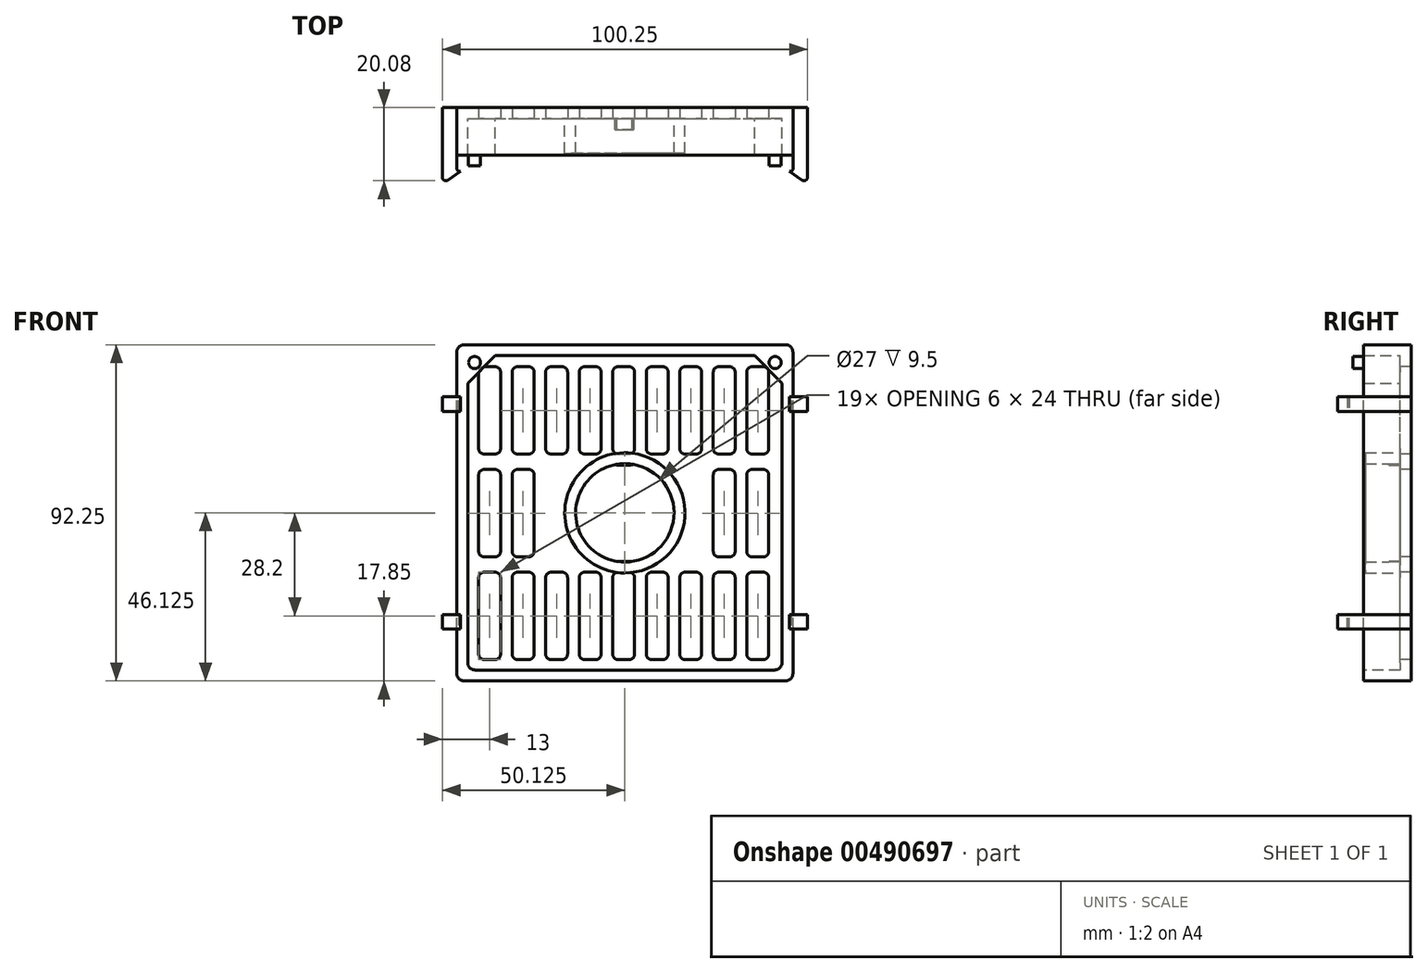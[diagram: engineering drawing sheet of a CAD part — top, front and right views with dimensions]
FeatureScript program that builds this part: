
annotation { "Feature Type Name" : "Feature", "Feature Type Description" : "" }
export const myFeature = defineFeature(function(context is Context, id is Id, definition is map)
    precondition{}
    {
        {
            var Q0;
            Q0=qCreatedBy(makeId("Front.planeOp"),FACE);
            var sketch = newSketch(context, id + "F0", { "sketchPlane" : qUnion([Q0])});
            skLineSegment(sketch, "E0.bottom", {"start": v(0, 0) * mm, "end": v(92.25, 0) * mm});
            skLineSegment(sketch, "E0.top", {"start": v(0, 92.25) * mm, "end": v(92.25, 92.25) * mm});
            skLineSegment(sketch, "E0.left", {"start": v(0, 0) * mm, "end": v(0, 92.25) * mm});
            skLineSegment(sketch, "E0.right", {"start": v(92.25, 0) * mm, "end": v(92.25, 92.25) * mm});
            skSolve(sketch);
        }
        {
            var Q0;
            Q0 = qSketchRegion(id + "F0", true);
            extrude(context, id + "F1", {"entities" : qUnion([Q0]), "depth" : 13 * mm, "offsetDistance" : 25 * mm});
        }
        {
            var Q0;
            Q0=makeQuery(id+"F1.opExtrude","SWEPT_EDGE",EDGE,{"disambiguationData":[OSD([sQuery(id+"F0.wireOp",EDGE,"E0.top"),sQuery(id+"F0.wireOp",EDGE,"E0.right")])]});
            var Q1;
            Q1=makeQuery(id+"F1.opExtrude","SWEPT_EDGE",EDGE,{"disambiguationData":[OSD([sQuery(id+"F0.wireOp",EDGE,"E0.top"),sQuery(id+"F0.wireOp",EDGE,"E0.left")])]});
            var Q2;
            Q2=makeQuery(id+"F1.opExtrude","SWEPT_EDGE",EDGE,{"disambiguationData":[OSD([sQuery(id+"F0.wireOp",EDGE,"E0.bottom"),sQuery(id+"F0.wireOp",EDGE,"E0.left")])]});
            var Q3;
            Q3=makeQuery(id+"F1.opExtrude","SWEPT_EDGE",EDGE,{"disambiguationData":[OSD([sQuery(id+"F0.wireOp",EDGE,"E0.bottom"),sQuery(id+"F0.wireOp",EDGE,"E0.right")])]});
            fillet(context, id + "F2", {"entities" : qUnion([Q0, Q1, Q2, Q3]), "radius" : 2 * mm, "tangentPropagation" : true, "allowEdgeOverflow" : false});
        }
        {
            var Q0;
            Q0=makeQuery(id+"F1.opExtrude","CAP_FACE",FACE,{"disambiguationData":[OSD([sQuery(id+"F0.wireOp",EDGE,"E0.bottom"),sQuery(id+"F0.wireOp",EDGE,"E0.top"),sQuery(id+"F0.wireOp",EDGE,"E0.left"),sQuery(id+"F0.wireOp",EDGE,"E0.right")])],"isStart":false});
            shell(context, id + "F3", {"entities" : qUnion([Q0]), "thickness" : 3 * mm});
        }
        {
            var Q0;
            Q0=makeQuery(id+"F3.opShell","OFFSET_FACE",FACE,{"disambiguationData":[OSD([sQuery(id+"F0.wireOp",EDGE,"E0.bottom"),sQuery(id+"F0.wireOp",EDGE,"E0.top"),sQuery(id+"F0.wireOp",EDGE,"E0.left"),sQuery(id+"F0.wireOp",EDGE,"E0.right")])]});
            var sketch = newSketch(context, id + "F4", { "sketchPlane" : qUnion([Q0])});
            skLineSegment(sketch, "E1", {"start": v(46.12, 89.25) * mm, "end": v(46.12, 3) * mm, "construction": true});
            skLineSegment(sketch, "E2", {"start": v(3, 46.12) * mm, "end": v(89.25, 46.12) * mm, "construction": true});
            skCircle(sketch, "E3", {"center": v(46.12, 46.12) * mm, "radius": 16.5 * mm});
            skSolve(sketch);
        }
        {
            var Q0;
            Q0 = qSketchRegion(id + "F4", true);
            extrude(context, id + "F5", {"entities" : qUnion([Q0]), "operationType" : NewBodyOperationType.ADD, "depth" : 9.5 * mm, "offsetDistance" : 25 * mm});
        }
        {
            var Q0;
            Q0=makeQuery(id+"F3.opShell","OFFSET_FACE",FACE,{"disambiguationData":[OSD([sQuery(id+"F0.wireOp",EDGE,"E0.bottom"),sQuery(id+"F0.wireOp",EDGE,"E0.top"),sQuery(id+"F0.wireOp",EDGE,"E0.left"),sQuery(id+"F0.wireOp",EDGE,"E0.right")])]});
            var sketch = newSketch(context, id + "F6", { "sketchPlane" : qUnion([Q0])});
            skLineSegment(sketch, "E4.bottom", {"start": v(7.5, 62.25) * mm, "end": v(10.5, 62.25) * mm});
            skLineSegment(sketch, "E4.top", {"start": v(7.5, 86.25) * mm, "end": v(10.5, 86.25) * mm});
            skLineSegment(sketch, "E4.left", {"start": v(6, 63.75) * mm, "end": v(6, 84.75) * mm});
            skLineSegment(sketch, "E4.right", {"start": v(12, 63.75) * mm, "end": v(12, 84.75) * mm});
            skPoint(sketch, "E5.visualSharp", {"position": v(6, 86.25) * mm});
            skArc(sketch, "E5.filletArc", {"start": v(7.5, 86.25) * mm, "mid": v(6.44, 85.81) * mm, "end": v(6, 84.75) * mm});
            skPoint(sketch, "E6.visualSharp", {"position": v(12, 62.25) * mm});
            skArc(sketch, "E6.filletArc", {"start": v(10.5, 62.25) * mm, "mid": v(11.56, 62.69) * mm, "end": v(12, 63.75) * mm});
            skPoint(sketch, "E7.visualSharp", {"position": v(6, 62.25) * mm});
            skArc(sketch, "E7.filletArc", {"start": v(6, 63.75) * mm, "mid": v(6.44, 62.69) * mm, "end": v(7.5, 62.25) * mm});
            skPoint(sketch, "E8.visualSharp", {"position": v(12, 86.25) * mm});
            skArc(sketch, "E8.filletArc", {"start": v(12, 84.75) * mm, "mid": v(11.56, 85.81) * mm, "end": v(10.5, 86.25) * mm});
            skPoint(sketch, "E9.0.1.0", {"position": v(12, 34.05) * mm});
            skPoint(sketch, "E9.0.1.1", {"position": v(6, 34.05) * mm});
            skPoint(sketch, "E9.0.1.2", {"position": v(12, 58.05) * mm});
            skLineSegment(sketch, "E9.0.1.3", {"start": v(12, 35.55) * mm, "end": v(12, 56.55) * mm});
            skPoint(sketch, "E9.0.1.4", {"position": v(6, 58.05) * mm});
            skLineSegment(sketch, "E9.0.1.5", {"start": v(6, 35.55) * mm, "end": v(6, 56.55) * mm});
            skLineSegment(sketch, "E9.0.1.6", {"start": v(7.5, 34.05) * mm, "end": v(10.5, 34.05) * mm});
            skArc(sketch, "E9.0.1.7", {"start": v(7.5, 58.05) * mm, "mid": v(6.44, 57.61) * mm, "end": v(6, 56.55) * mm});
            skArc(sketch, "E9.0.1.8", {"start": v(10.5, 34.05) * mm, "mid": v(11.56, 34.49) * mm, "end": v(12, 35.55) * mm});
            skLineSegment(sketch, "E9.0.1.9", {"start": v(7.5, 58.05) * mm, "end": v(10.5, 58.05) * mm});
            skArc(sketch, "E9.0.1.10", {"start": v(12, 56.55) * mm, "mid": v(11.56, 57.61) * mm, "end": v(10.5, 58.05) * mm});
            skArc(sketch, "E9.0.1.11", {"start": v(6, 35.55) * mm, "mid": v(6.44, 34.49) * mm, "end": v(7.5, 34.05) * mm});
            skPoint(sketch, "E9.0.2.0", {"position": v(12, 5.85) * mm});
            skPoint(sketch, "E9.0.2.1", {"position": v(6, 5.85) * mm});
            skPoint(sketch, "E9.0.2.2", {"position": v(12, 29.85) * mm});
            skLineSegment(sketch, "E9.0.2.3", {"start": v(12, 7.35) * mm, "end": v(12, 28.35) * mm});
            skPoint(sketch, "E9.0.2.4", {"position": v(6, 29.85) * mm});
            skLineSegment(sketch, "E9.0.2.5", {"start": v(6, 7.35) * mm, "end": v(6, 28.35) * mm});
            skLineSegment(sketch, "E9.0.2.6", {"start": v(7.5, 5.85) * mm, "end": v(10.5, 5.85) * mm});
            skArc(sketch, "E9.0.2.7", {"start": v(7.5, 29.85) * mm, "mid": v(6.44, 29.41) * mm, "end": v(6, 28.35) * mm});
            skArc(sketch, "E9.0.2.8", {"start": v(10.5, 5.85) * mm, "mid": v(11.56, 6.29) * mm, "end": v(12, 7.35) * mm});
            skLineSegment(sketch, "E9.0.2.9", {"start": v(7.5, 29.85) * mm, "end": v(10.5, 29.85) * mm});
            skArc(sketch, "E9.0.2.10", {"start": v(12, 28.35) * mm, "mid": v(11.56, 29.41) * mm, "end": v(10.5, 29.85) * mm});
            skArc(sketch, "E9.0.2.11", {"start": v(6, 7.35) * mm, "mid": v(6.44, 6.29) * mm, "end": v(7.5, 5.85) * mm});
            skPoint(sketch, "E9.1.0.0", {"position": v(21.2, 62.25) * mm});
            skPoint(sketch, "E9.1.0.1", {"position": v(15.2, 62.25) * mm});
            skPoint(sketch, "E9.1.0.2", {"position": v(21.2, 86.25) * mm});
            skLineSegment(sketch, "E9.1.0.3", {"start": v(21.2, 63.75) * mm, "end": v(21.2, 84.75) * mm});
            skPoint(sketch, "E9.1.0.4", {"position": v(15.2, 86.25) * mm});
            skLineSegment(sketch, "E9.1.0.5", {"start": v(15.2, 63.75) * mm, "end": v(15.2, 84.75) * mm});
            skLineSegment(sketch, "E9.1.0.6", {"start": v(16.7, 62.25) * mm, "end": v(19.7, 62.25) * mm});
            skArc(sketch, "E9.1.0.7", {"start": v(16.7, 86.25) * mm, "mid": v(15.64, 85.81) * mm, "end": v(15.2, 84.75) * mm});
            skArc(sketch, "E9.1.0.8", {"start": v(19.7, 62.25) * mm, "mid": v(20.76, 62.69) * mm, "end": v(21.2, 63.75) * mm});
            skLineSegment(sketch, "E9.1.0.9", {"start": v(16.7, 86.25) * mm, "end": v(19.7, 86.25) * mm});
            skArc(sketch, "E9.1.0.10", {"start": v(21.2, 84.75) * mm, "mid": v(20.76, 85.81) * mm, "end": v(19.7, 86.25) * mm});
            skArc(sketch, "E9.1.0.11", {"start": v(15.2, 63.75) * mm, "mid": v(15.64, 62.69) * mm, "end": v(16.7, 62.25) * mm});
            skPoint(sketch, "E9.1.1.0", {"position": v(21.2, 34.05) * mm});
            skPoint(sketch, "E9.1.1.1", {"position": v(15.2, 34.05) * mm});
            skPoint(sketch, "E9.1.1.2", {"position": v(21.2, 58.05) * mm});
            skLineSegment(sketch, "E9.1.1.3", {"start": v(21.2, 35.55) * mm, "end": v(21.2, 56.55) * mm});
            skPoint(sketch, "E9.1.1.4", {"position": v(15.2, 58.05) * mm});
            skLineSegment(sketch, "E9.1.1.5", {"start": v(15.2, 35.55) * mm, "end": v(15.2, 56.55) * mm});
            skLineSegment(sketch, "E9.1.1.6", {"start": v(16.7, 34.05) * mm, "end": v(19.7, 34.05) * mm});
            skArc(sketch, "E9.1.1.7", {"start": v(16.7, 58.05) * mm, "mid": v(15.64, 57.61) * mm, "end": v(15.2, 56.55) * mm});
            skArc(sketch, "E9.1.1.8", {"start": v(19.7, 34.05) * mm, "mid": v(20.76, 34.49) * mm, "end": v(21.2, 35.55) * mm});
            skLineSegment(sketch, "E9.1.1.9", {"start": v(16.7, 58.05) * mm, "end": v(19.7, 58.05) * mm});
            skArc(sketch, "E9.1.1.10", {"start": v(21.2, 56.55) * mm, "mid": v(20.76, 57.61) * mm, "end": v(19.7, 58.05) * mm});
            skArc(sketch, "E9.1.1.11", {"start": v(15.2, 35.55) * mm, "mid": v(15.64, 34.49) * mm, "end": v(16.7, 34.05) * mm});
            skPoint(sketch, "E9.1.2.0", {"position": v(21.2, 5.85) * mm});
            skPoint(sketch, "E9.1.2.1", {"position": v(15.2, 5.85) * mm});
            skPoint(sketch, "E9.1.2.2", {"position": v(21.2, 29.85) * mm});
            skLineSegment(sketch, "E9.1.2.3", {"start": v(21.2, 7.35) * mm, "end": v(21.2, 28.35) * mm});
            skPoint(sketch, "E9.1.2.4", {"position": v(15.2, 29.85) * mm});
            skLineSegment(sketch, "E9.1.2.5", {"start": v(15.2, 7.35) * mm, "end": v(15.2, 28.35) * mm});
            skLineSegment(sketch, "E9.1.2.6", {"start": v(16.7, 5.85) * mm, "end": v(19.7, 5.85) * mm});
            skArc(sketch, "E9.1.2.7", {"start": v(16.7, 29.85) * mm, "mid": v(15.64, 29.41) * mm, "end": v(15.2, 28.35) * mm});
            skArc(sketch, "E9.1.2.8", {"start": v(19.7, 5.85) * mm, "mid": v(20.76, 6.29) * mm, "end": v(21.2, 7.35) * mm});
            skLineSegment(sketch, "E9.1.2.9", {"start": v(16.7, 29.85) * mm, "end": v(19.7, 29.85) * mm});
            skArc(sketch, "E9.1.2.10", {"start": v(21.2, 28.35) * mm, "mid": v(20.76, 29.41) * mm, "end": v(19.7, 29.85) * mm});
            skArc(sketch, "E9.1.2.11", {"start": v(15.2, 7.35) * mm, "mid": v(15.64, 6.29) * mm, "end": v(16.7, 5.85) * mm});
            skPoint(sketch, "E9.2.0.0", {"position": v(30.4, 62.25) * mm});
            skPoint(sketch, "E9.2.0.1", {"position": v(24.4, 62.25) * mm});
            skPoint(sketch, "E9.2.0.2", {"position": v(30.4, 86.25) * mm});
            skLineSegment(sketch, "E9.2.0.3", {"start": v(30.4, 63.75) * mm, "end": v(30.4, 84.75) * mm});
            skPoint(sketch, "E9.2.0.4", {"position": v(24.4, 86.25) * mm});
            skLineSegment(sketch, "E9.2.0.5", {"start": v(24.4, 63.75) * mm, "end": v(24.4, 84.75) * mm});
            skLineSegment(sketch, "E9.2.0.6", {"start": v(25.9, 62.25) * mm, "end": v(28.9, 62.25) * mm});
            skArc(sketch, "E9.2.0.7", {"start": v(25.9, 86.25) * mm, "mid": v(24.84, 85.81) * mm, "end": v(24.4, 84.75) * mm});
            skArc(sketch, "E9.2.0.8", {"start": v(28.9, 62.25) * mm, "mid": v(29.96, 62.69) * mm, "end": v(30.4, 63.75) * mm});
            skLineSegment(sketch, "E9.2.0.9", {"start": v(25.9, 86.25) * mm, "end": v(28.9, 86.25) * mm});
            skArc(sketch, "E9.2.0.10", {"start": v(30.4, 84.75) * mm, "mid": v(29.96, 85.81) * mm, "end": v(28.9, 86.25) * mm});
            skArc(sketch, "E9.2.0.11", {"start": v(24.4, 63.75) * mm, "mid": v(24.84, 62.69) * mm, "end": v(25.9, 62.25) * mm});
            skPoint(sketch, "E9.2.1.0", {"position": v(30.4, 34.05) * mm});
            skPoint(sketch, "E9.2.1.1", {"position": v(24.4, 34.05) * mm});
            skPoint(sketch, "E9.2.1.2", {"position": v(30.4, 58.05) * mm});
            skLineSegment(sketch, "E9.2.1.3", {"start": v(30.4, 35.55) * mm, "end": v(30.4, 41.13) * mm});
            skPoint(sketch, "E9.2.1.4", {"position": v(24.4, 58.05) * mm});
            skLineSegment(sketch, "E9.2.1.5", {"start": v(24.4, 35.55) * mm, "end": v(24.4, 56.55) * mm});
            skLineSegment(sketch, "E9.2.1.6", {"start": v(25.9, 34.05) * mm, "end": v(28.9, 34.05) * mm});
            skArc(sketch, "E9.2.1.7", {"start": v(25.9, 58.05) * mm, "mid": v(24.84, 57.61) * mm, "end": v(24.4, 56.55) * mm});
            skArc(sketch, "E9.2.1.8", {"start": v(28.9, 34.05) * mm, "mid": v(29.96, 34.49) * mm, "end": v(30.4, 35.55) * mm});
            skLineSegment(sketch, "E9.2.1.9", {"start": v(25.9, 58.05) * mm, "end": v(28.9, 58.05) * mm});
            skArc(sketch, "E9.2.1.10", {"start": v(30.4, 56.55) * mm, "mid": v(29.96, 57.61) * mm, "end": v(28.9, 58.05) * mm});
            skArc(sketch, "E9.2.1.11", {"start": v(24.4, 35.55) * mm, "mid": v(24.84, 34.49) * mm, "end": v(25.9, 34.05) * mm});
            skPoint(sketch, "E9.2.2.0", {"position": v(30.4, 5.85) * mm});
            skPoint(sketch, "E9.2.2.1", {"position": v(24.4, 5.85) * mm});
            skPoint(sketch, "E9.2.2.2", {"position": v(30.4, 29.85) * mm});
            skLineSegment(sketch, "E9.2.2.3", {"start": v(30.4, 7.35) * mm, "end": v(30.4, 28.35) * mm});
            skPoint(sketch, "E9.2.2.4", {"position": v(24.4, 29.85) * mm});
            skLineSegment(sketch, "E9.2.2.5", {"start": v(24.4, 7.35) * mm, "end": v(24.4, 28.35) * mm});
            skLineSegment(sketch, "E9.2.2.6", {"start": v(25.9, 5.85) * mm, "end": v(28.9, 5.85) * mm});
            skArc(sketch, "E9.2.2.7", {"start": v(25.9, 29.85) * mm, "mid": v(24.84, 29.41) * mm, "end": v(24.4, 28.35) * mm});
            skArc(sketch, "E9.2.2.8", {"start": v(28.9, 5.85) * mm, "mid": v(29.96, 6.29) * mm, "end": v(30.4, 7.35) * mm});
            skLineSegment(sketch, "E9.2.2.9", {"start": v(25.9, 29.85) * mm, "end": v(28.9, 29.85) * mm});
            skArc(sketch, "E9.2.2.10", {"start": v(30.4, 28.35) * mm, "mid": v(29.96, 29.41) * mm, "end": v(28.9, 29.85) * mm});
            skArc(sketch, "E9.2.2.11", {"start": v(24.4, 7.35) * mm, "mid": v(24.84, 6.29) * mm, "end": v(25.9, 5.85) * mm});
            skPoint(sketch, "E9.3.0.0", {"position": v(39.6, 62.25) * mm});
            skPoint(sketch, "E9.3.0.1", {"position": v(33.6, 62.25) * mm});
            skPoint(sketch, "E9.3.0.2", {"position": v(39.6, 86.25) * mm});
            skLineSegment(sketch, "E9.3.0.3", {"start": v(39.6, 63.75) * mm, "end": v(39.6, 84.75) * mm});
            skPoint(sketch, "E9.3.0.4", {"position": v(33.6, 86.25) * mm});
            skLineSegment(sketch, "E9.3.0.5", {"start": v(33.6, 63.75) * mm, "end": v(33.6, 84.75) * mm});
            skLineSegment(sketch, "E9.3.0.6", {"start": v(35.1, 62.25) * mm, "end": v(38.1, 62.25) * mm});
            skArc(sketch, "E9.3.0.7", {"start": v(35.1, 86.25) * mm, "mid": v(34.04, 85.81) * mm, "end": v(33.6, 84.75) * mm});
            skArc(sketch, "E9.3.0.8", {"start": v(38.1, 62.25) * mm, "mid": v(39.16, 62.69) * mm, "end": v(39.6, 63.75) * mm});
            skLineSegment(sketch, "E9.3.0.9", {"start": v(35.1, 86.25) * mm, "end": v(38.1, 86.25) * mm});
            skArc(sketch, "E9.3.0.10", {"start": v(39.6, 84.75) * mm, "mid": v(39.16, 85.81) * mm, "end": v(38.1, 86.25) * mm});
            skArc(sketch, "E9.3.0.11", {"start": v(33.6, 63.75) * mm, "mid": v(34.04, 62.69) * mm, "end": v(35.1, 62.25) * mm});
            skPoint(sketch, "E9.3.2.0", {"position": v(39.6, 5.85) * mm});
            skPoint(sketch, "E9.3.2.1", {"position": v(33.6, 5.85) * mm});
            skPoint(sketch, "E9.3.2.2", {"position": v(39.6, 29.85) * mm});
            skLineSegment(sketch, "E9.3.2.3", {"start": v(39.6, 7.35) * mm, "end": v(39.6, 28.35) * mm});
            skPoint(sketch, "E9.3.2.4", {"position": v(33.6, 29.85) * mm});
            skLineSegment(sketch, "E9.3.2.5", {"start": v(33.6, 7.35) * mm, "end": v(33.6, 28.35) * mm});
            skLineSegment(sketch, "E9.3.2.6", {"start": v(35.1, 5.85) * mm, "end": v(38.1, 5.85) * mm});
            skArc(sketch, "E9.3.2.7", {"start": v(35.1, 29.85) * mm, "mid": v(34.04, 29.41) * mm, "end": v(33.6, 28.35) * mm});
            skArc(sketch, "E9.3.2.8", {"start": v(38.1, 5.85) * mm, "mid": v(39.16, 6.29) * mm, "end": v(39.6, 7.35) * mm});
            skLineSegment(sketch, "E9.3.2.9", {"start": v(35.1, 29.85) * mm, "end": v(38.1, 29.85) * mm});
            skArc(sketch, "E9.3.2.10", {"start": v(39.6, 28.35) * mm, "mid": v(39.16, 29.41) * mm, "end": v(38.1, 29.85) * mm});
            skArc(sketch, "E9.3.2.11", {"start": v(33.6, 7.35) * mm, "mid": v(34.04, 6.29) * mm, "end": v(35.1, 5.85) * mm});
            skPoint(sketch, "E9.4.0.0", {"position": v(48.8, 62.25) * mm});
            skPoint(sketch, "E9.4.0.1", {"position": v(42.8, 62.25) * mm});
            skPoint(sketch, "E9.4.0.2", {"position": v(48.8, 86.25) * mm});
            skLineSegment(sketch, "E9.4.0.3", {"start": v(48.8, 63.75) * mm, "end": v(48.8, 84.75) * mm});
            skPoint(sketch, "E9.4.0.4", {"position": v(42.8, 86.25) * mm});
            skLineSegment(sketch, "E9.4.0.5", {"start": v(42.8, 63.75) * mm, "end": v(42.8, 84.75) * mm});
            skLineSegment(sketch, "E9.4.0.6", {"start": v(44.3, 62.25) * mm, "end": v(47.3, 62.25) * mm});
            skArc(sketch, "E9.4.0.7", {"start": v(44.3, 86.25) * mm, "mid": v(43.24, 85.81) * mm, "end": v(42.8, 84.75) * mm});
            skArc(sketch, "E9.4.0.8", {"start": v(47.3, 62.25) * mm, "mid": v(48.36, 62.69) * mm, "end": v(48.8, 63.75) * mm});
            skLineSegment(sketch, "E9.4.0.9", {"start": v(44.3, 86.25) * mm, "end": v(47.3, 86.25) * mm});
            skArc(sketch, "E9.4.0.10", {"start": v(48.8, 84.75) * mm, "mid": v(48.36, 85.81) * mm, "end": v(47.3, 86.25) * mm});
            skArc(sketch, "E9.4.0.11", {"start": v(42.8, 63.75) * mm, "mid": v(43.24, 62.69) * mm, "end": v(44.3, 62.25) * mm});
            skPoint(sketch, "E9.4.2.0", {"position": v(48.8, 5.85) * mm});
            skPoint(sketch, "E9.4.2.1", {"position": v(42.8, 5.85) * mm});
            skPoint(sketch, "E9.4.2.2", {"position": v(48.8, 29.85) * mm});
            skLineSegment(sketch, "E9.4.2.3", {"start": v(48.8, 7.35) * mm, "end": v(48.8, 28.35) * mm});
            skPoint(sketch, "E9.4.2.4", {"position": v(42.8, 29.85) * mm});
            skLineSegment(sketch, "E9.4.2.5", {"start": v(42.8, 7.35) * mm, "end": v(42.8, 28.35) * mm});
            skLineSegment(sketch, "E9.4.2.6", {"start": v(44.3, 5.85) * mm, "end": v(47.3, 5.85) * mm});
            skArc(sketch, "E9.4.2.7", {"start": v(44.3, 29.85) * mm, "mid": v(43.24, 29.41) * mm, "end": v(42.8, 28.35) * mm});
            skArc(sketch, "E9.4.2.8", {"start": v(47.3, 5.85) * mm, "mid": v(48.36, 6.29) * mm, "end": v(48.8, 7.35) * mm});
            skLineSegment(sketch, "E9.4.2.9", {"start": v(44.3, 29.85) * mm, "end": v(47.3, 29.85) * mm});
            skArc(sketch, "E9.4.2.10", {"start": v(48.8, 28.35) * mm, "mid": v(48.36, 29.41) * mm, "end": v(47.3, 29.85) * mm});
            skArc(sketch, "E9.4.2.11", {"start": v(42.8, 7.35) * mm, "mid": v(43.24, 6.29) * mm, "end": v(44.3, 5.85) * mm});
            skPoint(sketch, "E9.5.0.0", {"position": v(58, 62.25) * mm});
            skPoint(sketch, "E9.5.0.1", {"position": v(52, 62.25) * mm});
            skPoint(sketch, "E9.5.0.2", {"position": v(58, 86.25) * mm});
            skLineSegment(sketch, "E9.5.0.3", {"start": v(58, 63.75) * mm, "end": v(58, 84.75) * mm});
            skPoint(sketch, "E9.5.0.4", {"position": v(52, 86.25) * mm});
            skLineSegment(sketch, "E9.5.0.5", {"start": v(52, 63.75) * mm, "end": v(52, 84.75) * mm});
            skLineSegment(sketch, "E9.5.0.6", {"start": v(53.5, 62.25) * mm, "end": v(56.5, 62.25) * mm});
            skArc(sketch, "E9.5.0.7", {"start": v(53.5, 86.25) * mm, "mid": v(52.44, 85.81) * mm, "end": v(52, 84.75) * mm});
            skArc(sketch, "E9.5.0.8", {"start": v(56.5, 62.25) * mm, "mid": v(57.56, 62.69) * mm, "end": v(58, 63.75) * mm});
            skLineSegment(sketch, "E9.5.0.9", {"start": v(53.5, 86.25) * mm, "end": v(56.5, 86.25) * mm});
            skArc(sketch, "E9.5.0.10", {"start": v(58, 84.75) * mm, "mid": v(57.56, 85.81) * mm, "end": v(56.5, 86.25) * mm});
            skArc(sketch, "E9.5.0.11", {"start": v(52, 63.75) * mm, "mid": v(52.44, 62.69) * mm, "end": v(53.5, 62.25) * mm});
            skPoint(sketch, "E9.5.2.0", {"position": v(58, 5.85) * mm});
            skPoint(sketch, "E9.5.2.1", {"position": v(52, 5.85) * mm});
            skPoint(sketch, "E9.5.2.2", {"position": v(58, 29.85) * mm});
            skLineSegment(sketch, "E9.5.2.3", {"start": v(58, 7.35) * mm, "end": v(58, 28.35) * mm});
            skPoint(sketch, "E9.5.2.4", {"position": v(52, 29.85) * mm});
            skLineSegment(sketch, "E9.5.2.5", {"start": v(52, 7.35) * mm, "end": v(52, 28.35) * mm});
            skLineSegment(sketch, "E9.5.2.6", {"start": v(53.5, 5.85) * mm, "end": v(56.5, 5.85) * mm});
            skArc(sketch, "E9.5.2.7", {"start": v(53.5, 29.85) * mm, "mid": v(52.44, 29.41) * mm, "end": v(52, 28.35) * mm});
            skArc(sketch, "E9.5.2.8", {"start": v(56.5, 5.85) * mm, "mid": v(57.56, 6.29) * mm, "end": v(58, 7.35) * mm});
            skLineSegment(sketch, "E9.5.2.9", {"start": v(53.5, 29.85) * mm, "end": v(56.5, 29.85) * mm});
            skArc(sketch, "E9.5.2.10", {"start": v(58, 28.35) * mm, "mid": v(57.56, 29.41) * mm, "end": v(56.5, 29.85) * mm});
            skArc(sketch, "E9.5.2.11", {"start": v(52, 7.35) * mm, "mid": v(52.44, 6.29) * mm, "end": v(53.5, 5.85) * mm});
            skPoint(sketch, "E9.6.0.0", {"position": v(67.2, 62.25) * mm});
            skPoint(sketch, "E9.6.0.1", {"position": v(61.2, 62.25) * mm});
            skPoint(sketch, "E9.6.0.2", {"position": v(67.2, 86.25) * mm});
            skLineSegment(sketch, "E9.6.0.3", {"start": v(67.2, 63.75) * mm, "end": v(67.2, 84.75) * mm});
            skPoint(sketch, "E9.6.0.4", {"position": v(61.2, 86.25) * mm});
            skLineSegment(sketch, "E9.6.0.5", {"start": v(61.2, 63.75) * mm, "end": v(61.2, 84.75) * mm});
            skLineSegment(sketch, "E9.6.0.6", {"start": v(62.7, 62.25) * mm, "end": v(65.7, 62.25) * mm});
            skArc(sketch, "E9.6.0.7", {"start": v(62.7, 86.25) * mm, "mid": v(61.64, 85.81) * mm, "end": v(61.2, 84.75) * mm});
            skArc(sketch, "E9.6.0.8", {"start": v(65.7, 62.25) * mm, "mid": v(66.76, 62.69) * mm, "end": v(67.2, 63.75) * mm});
            skLineSegment(sketch, "E9.6.0.9", {"start": v(62.7, 86.25) * mm, "end": v(65.7, 86.25) * mm});
            skArc(sketch, "E9.6.0.10", {"start": v(67.2, 84.75) * mm, "mid": v(66.76, 85.81) * mm, "end": v(65.7, 86.25) * mm});
            skArc(sketch, "E9.6.0.11", {"start": v(61.2, 63.75) * mm, "mid": v(61.64, 62.69) * mm, "end": v(62.7, 62.25) * mm});
            skPoint(sketch, "E9.6.1.0", {"position": v(67.2, 34.05) * mm});
            skPoint(sketch, "E9.6.1.1", {"position": v(61.2, 34.05) * mm});
            skPoint(sketch, "E9.6.1.2", {"position": v(67.2, 58.05) * mm});
            skLineSegment(sketch, "E9.6.1.3", {"start": v(67.2, 35.55) * mm, "end": v(67.2, 56.55) * mm});
            skPoint(sketch, "E9.6.1.4", {"position": v(61.2, 58.05) * mm});
            skLineSegment(sketch, "E9.6.1.5", {"start": v(61.2, 35.55) * mm, "end": v(61.2, 39.42) * mm});
            skLineSegment(sketch, "E9.6.1.6", {"start": v(62.7, 34.05) * mm, "end": v(65.7, 34.05) * mm});
            skArc(sketch, "E9.6.1.7", {"start": v(62.7, 58.05) * mm, "mid": v(61.64, 57.61) * mm, "end": v(61.2, 56.55) * mm});
            skArc(sketch, "E9.6.1.8", {"start": v(65.7, 34.05) * mm, "mid": v(66.76, 34.49) * mm, "end": v(67.2, 35.55) * mm});
            skLineSegment(sketch, "E9.6.1.9", {"start": v(62.7, 58.05) * mm, "end": v(65.7, 58.05) * mm});
            skArc(sketch, "E9.6.1.10", {"start": v(67.2, 56.55) * mm, "mid": v(66.76, 57.61) * mm, "end": v(65.7, 58.05) * mm});
            skArc(sketch, "E9.6.1.11", {"start": v(61.2, 35.55) * mm, "mid": v(61.64, 34.49) * mm, "end": v(62.7, 34.05) * mm});
            skPoint(sketch, "E9.6.2.0", {"position": v(67.2, 5.85) * mm});
            skPoint(sketch, "E9.6.2.1", {"position": v(61.2, 5.85) * mm});
            skPoint(sketch, "E9.6.2.2", {"position": v(67.2, 29.85) * mm});
            skLineSegment(sketch, "E9.6.2.3", {"start": v(67.2, 7.35) * mm, "end": v(67.2, 28.35) * mm});
            skPoint(sketch, "E9.6.2.4", {"position": v(61.2, 29.85) * mm});
            skLineSegment(sketch, "E9.6.2.5", {"start": v(61.2, 7.35) * mm, "end": v(61.2, 28.35) * mm});
            skLineSegment(sketch, "E9.6.2.6", {"start": v(62.7, 5.85) * mm, "end": v(65.7, 5.85) * mm});
            skArc(sketch, "E9.6.2.7", {"start": v(62.7, 29.85) * mm, "mid": v(61.64, 29.41) * mm, "end": v(61.2, 28.35) * mm});
            skArc(sketch, "E9.6.2.8", {"start": v(65.7, 5.85) * mm, "mid": v(66.76, 6.29) * mm, "end": v(67.2, 7.35) * mm});
            skLineSegment(sketch, "E9.6.2.9", {"start": v(62.7, 29.85) * mm, "end": v(65.7, 29.85) * mm});
            skArc(sketch, "E9.6.2.10", {"start": v(67.2, 28.35) * mm, "mid": v(66.76, 29.41) * mm, "end": v(65.7, 29.85) * mm});
            skArc(sketch, "E9.6.2.11", {"start": v(61.2, 7.35) * mm, "mid": v(61.64, 6.29) * mm, "end": v(62.7, 5.85) * mm});
            skPoint(sketch, "E9.7.0.0", {"position": v(76.4, 62.25) * mm});
            skPoint(sketch, "E9.7.0.1", {"position": v(70.4, 62.25) * mm});
            skPoint(sketch, "E9.7.0.2", {"position": v(76.4, 86.25) * mm});
            skLineSegment(sketch, "E9.7.0.3", {"start": v(76.4, 63.75) * mm, "end": v(76.4, 84.75) * mm});
            skPoint(sketch, "E9.7.0.4", {"position": v(70.4, 86.25) * mm});
            skLineSegment(sketch, "E9.7.0.5", {"start": v(70.4, 63.75) * mm, "end": v(70.4, 84.75) * mm});
            skLineSegment(sketch, "E9.7.0.6", {"start": v(71.9, 62.25) * mm, "end": v(74.9, 62.25) * mm});
            skArc(sketch, "E9.7.0.7", {"start": v(71.9, 86.25) * mm, "mid": v(70.84, 85.81) * mm, "end": v(70.4, 84.75) * mm});
            skArc(sketch, "E9.7.0.8", {"start": v(74.9, 62.25) * mm, "mid": v(75.96, 62.69) * mm, "end": v(76.4, 63.75) * mm});
            skLineSegment(sketch, "E9.7.0.9", {"start": v(71.9, 86.25) * mm, "end": v(74.9, 86.25) * mm});
            skArc(sketch, "E9.7.0.10", {"start": v(76.4, 84.75) * mm, "mid": v(75.96, 85.81) * mm, "end": v(74.9, 86.25) * mm});
            skArc(sketch, "E9.7.0.11", {"start": v(70.4, 63.75) * mm, "mid": v(70.84, 62.69) * mm, "end": v(71.9, 62.25) * mm});
            skPoint(sketch, "E9.7.1.0", {"position": v(76.4, 34.05) * mm});
            skPoint(sketch, "E9.7.1.1", {"position": v(70.4, 34.05) * mm});
            skPoint(sketch, "E9.7.1.2", {"position": v(76.4, 58.05) * mm});
            skLineSegment(sketch, "E9.7.1.3", {"start": v(76.4, 35.55) * mm, "end": v(76.4, 56.55) * mm});
            skPoint(sketch, "E9.7.1.4", {"position": v(70.4, 58.05) * mm});
            skLineSegment(sketch, "E9.7.1.5", {"start": v(70.4, 35.55) * mm, "end": v(70.4, 56.55) * mm});
            skLineSegment(sketch, "E9.7.1.6", {"start": v(71.9, 34.05) * mm, "end": v(74.9, 34.05) * mm});
            skArc(sketch, "E9.7.1.7", {"start": v(71.9, 58.05) * mm, "mid": v(70.84, 57.61) * mm, "end": v(70.4, 56.55) * mm});
            skArc(sketch, "E9.7.1.8", {"start": v(74.9, 34.05) * mm, "mid": v(75.96, 34.49) * mm, "end": v(76.4, 35.55) * mm});
            skLineSegment(sketch, "E9.7.1.9", {"start": v(71.9, 58.05) * mm, "end": v(74.9, 58.05) * mm});
            skArc(sketch, "E9.7.1.10", {"start": v(76.4, 56.55) * mm, "mid": v(75.96, 57.61) * mm, "end": v(74.9, 58.05) * mm});
            skArc(sketch, "E9.7.1.11", {"start": v(70.4, 35.55) * mm, "mid": v(70.84, 34.49) * mm, "end": v(71.9, 34.05) * mm});
            skPoint(sketch, "E9.7.2.0", {"position": v(76.4, 5.85) * mm});
            skPoint(sketch, "E9.7.2.1", {"position": v(70.4, 5.85) * mm});
            skPoint(sketch, "E9.7.2.2", {"position": v(76.4, 29.85) * mm});
            skLineSegment(sketch, "E9.7.2.3", {"start": v(76.4, 7.35) * mm, "end": v(76.4, 28.35) * mm});
            skPoint(sketch, "E9.7.2.4", {"position": v(70.4, 29.85) * mm});
            skLineSegment(sketch, "E9.7.2.5", {"start": v(70.4, 7.35) * mm, "end": v(70.4, 28.35) * mm});
            skLineSegment(sketch, "E9.7.2.6", {"start": v(71.9, 5.85) * mm, "end": v(74.9, 5.85) * mm});
            skArc(sketch, "E9.7.2.7", {"start": v(71.9, 29.85) * mm, "mid": v(70.84, 29.41) * mm, "end": v(70.4, 28.35) * mm});
            skArc(sketch, "E9.7.2.8", {"start": v(74.9, 5.85) * mm, "mid": v(75.96, 6.29) * mm, "end": v(76.4, 7.35) * mm});
            skLineSegment(sketch, "E9.7.2.9", {"start": v(71.9, 29.85) * mm, "end": v(74.9, 29.85) * mm});
            skArc(sketch, "E9.7.2.10", {"start": v(76.4, 28.35) * mm, "mid": v(75.96, 29.41) * mm, "end": v(74.9, 29.85) * mm});
            skArc(sketch, "E9.7.2.11", {"start": v(70.4, 7.35) * mm, "mid": v(70.84, 6.29) * mm, "end": v(71.9, 5.85) * mm});
            skPoint(sketch, "E9.8.0.0", {"position": v(85.6, 62.25) * mm});
            skPoint(sketch, "E9.8.0.1", {"position": v(79.6, 62.25) * mm});
            skPoint(sketch, "E9.8.0.2", {"position": v(85.6, 86.25) * mm});
            skLineSegment(sketch, "E9.8.0.3", {"start": v(85.6, 63.75) * mm, "end": v(85.6, 84.75) * mm});
            skPoint(sketch, "E9.8.0.4", {"position": v(79.6, 86.25) * mm});
            skLineSegment(sketch, "E9.8.0.5", {"start": v(79.6, 63.75) * mm, "end": v(79.6, 84.75) * mm});
            skLineSegment(sketch, "E9.8.0.6", {"start": v(81.1, 62.25) * mm, "end": v(84.1, 62.25) * mm});
            skArc(sketch, "E9.8.0.7", {"start": v(81.1, 86.25) * mm, "mid": v(80.04, 85.81) * mm, "end": v(79.6, 84.75) * mm});
            skArc(sketch, "E9.8.0.8", {"start": v(84.1, 62.25) * mm, "mid": v(85.16, 62.69) * mm, "end": v(85.6, 63.75) * mm});
            skLineSegment(sketch, "E9.8.0.9", {"start": v(81.1, 86.25) * mm, "end": v(84.1, 86.25) * mm});
            skArc(sketch, "E9.8.0.10", {"start": v(85.6, 84.75) * mm, "mid": v(85.16, 85.81) * mm, "end": v(84.1, 86.25) * mm});
            skArc(sketch, "E9.8.0.11", {"start": v(79.6, 63.75) * mm, "mid": v(80.04, 62.69) * mm, "end": v(81.1, 62.25) * mm});
            skPoint(sketch, "E9.8.1.0", {"position": v(85.6, 34.05) * mm});
            skPoint(sketch, "E9.8.1.1", {"position": v(79.6, 34.05) * mm});
            skPoint(sketch, "E9.8.1.2", {"position": v(85.6, 58.05) * mm});
            skLineSegment(sketch, "E9.8.1.3", {"start": v(85.6, 35.55) * mm, "end": v(85.6, 56.55) * mm});
            skPoint(sketch, "E9.8.1.4", {"position": v(79.6, 58.05) * mm});
            skLineSegment(sketch, "E9.8.1.5", {"start": v(79.6, 35.55) * mm, "end": v(79.6, 56.55) * mm});
            skLineSegment(sketch, "E9.8.1.6", {"start": v(81.1, 34.05) * mm, "end": v(84.1, 34.05) * mm});
            skArc(sketch, "E9.8.1.7", {"start": v(81.1, 58.05) * mm, "mid": v(80.04, 57.61) * mm, "end": v(79.6, 56.55) * mm});
            skArc(sketch, "E9.8.1.8", {"start": v(84.1, 34.05) * mm, "mid": v(85.16, 34.49) * mm, "end": v(85.6, 35.55) * mm});
            skLineSegment(sketch, "E9.8.1.9", {"start": v(81.1, 58.05) * mm, "end": v(84.1, 58.05) * mm});
            skArc(sketch, "E9.8.1.10", {"start": v(85.6, 56.55) * mm, "mid": v(85.16, 57.61) * mm, "end": v(84.1, 58.05) * mm});
            skArc(sketch, "E9.8.1.11", {"start": v(79.6, 35.55) * mm, "mid": v(80.04, 34.49) * mm, "end": v(81.1, 34.05) * mm});
            skPoint(sketch, "E9.8.2.0", {"position": v(85.6, 5.85) * mm});
            skPoint(sketch, "E9.8.2.1", {"position": v(79.6, 5.85) * mm});
            skPoint(sketch, "E9.8.2.2", {"position": v(85.6, 29.85) * mm});
            skLineSegment(sketch, "E9.8.2.3", {"start": v(85.6, 7.35) * mm, "end": v(85.6, 28.35) * mm});
            skPoint(sketch, "E9.8.2.4", {"position": v(79.6, 29.85) * mm});
            skLineSegment(sketch, "E9.8.2.5", {"start": v(79.6, 7.35) * mm, "end": v(79.6, 28.35) * mm});
            skLineSegment(sketch, "E9.8.2.6", {"start": v(81.1, 5.85) * mm, "end": v(84.1, 5.85) * mm});
            skArc(sketch, "E9.8.2.7", {"start": v(81.1, 29.85) * mm, "mid": v(80.04, 29.41) * mm, "end": v(79.6, 28.35) * mm});
            skArc(sketch, "E9.8.2.8", {"start": v(84.1, 5.85) * mm, "mid": v(85.16, 6.29) * mm, "end": v(85.6, 7.35) * mm});
            skLineSegment(sketch, "E9.8.2.9", {"start": v(81.1, 29.85) * mm, "end": v(84.1, 29.85) * mm});
            skArc(sketch, "E9.8.2.10", {"start": v(85.6, 28.35) * mm, "mid": v(85.16, 29.41) * mm, "end": v(84.1, 29.85) * mm});
            skArc(sketch, "E9.8.2.11", {"start": v(79.6, 7.35) * mm, "mid": v(80.04, 6.29) * mm, "end": v(81.1, 5.85) * mm});
            skLineSegment(sketch, "E9.direction1", {"start": v(6, 62.25) * mm, "end": v(15.2, 62.25) * mm, "construction": true});
            skLineSegment(sketch, "E9.direction2", {"start": v(6, 62.25) * mm, "end": v(6, 34.05) * mm, "construction": true});
            skCircle(sketch, "E10.0", {"center": v(46.12, 46.12) * mm, "radius": 16.5 * mm, "construction": true});
            skLineSegment(sketch, "E11.trimOffspring", {"start": v(30.4, 51.12) * mm, "end": v(30.4, 56.55) * mm});
            skLineSegment(sketch, "E12.trimOffspring", {"start": v(61.2, 52.83) * mm, "end": v(61.2, 56.55) * mm});
            skSolve(sketch);
        }
        {
            var Q0;
            Q0 = qSketchRegion(id + "F6", true);
            extrude(context, id + "F7", {"entities" : qUnion([Q0]), "operationType" : NewBodyOperationType.REMOVE, "endBound" : BoundingType.THROUGH_ALL, "oppositeDirection" : true, "depth" : 25 * mm, "offsetDistance" : 25 * mm});
        }
        {
            var Q0;
            Q0=makeQuery(id+"F3.opShell","OFFSET_EDGE",EDGE,{"disambiguationData":[OSD([sQuery(id+"F0.wireOp",EDGE,"E0.top"),sQuery(id+"F0.wireOp",EDGE,"E0.left")])]});
            var Q1;
            Q1=makeQuery(id+"F3.opShell","OFFSET_EDGE",EDGE,{"disambiguationData":[OSD([sQuery(id+"F0.wireOp",EDGE,"E0.top"),sQuery(id+"F0.wireOp",EDGE,"E0.right")])]});
            var Q2;
            Q2=makeQuery(id+"F3.opShell","OFFSET_EDGE",EDGE,{"disambiguationData":[OSD([sQuery(id+"F0.wireOp",EDGE,"E0.bottom"),sQuery(id+"F0.wireOp",EDGE,"E0.right")])]});
            var Q3;
            Q3=makeQuery(id+"F3.opShell","OFFSET_EDGE",EDGE,{"disambiguationData":[OSD([sQuery(id+"F0.wireOp",EDGE,"E0.bottom"),sQuery(id+"F0.wireOp",EDGE,"E0.left")])]});
            fillet(context, id + "F8", {"entities" : qUnion([Q0, Q1, Q2, Q3]), "radius" : 2 * mm, "tangentPropagation" : true, "allowEdgeOverflow" : false});
        }
        {
            var Q0;
            Q0=makeQuery(id+"F5.opExtrude","CAP_FACE",FACE,{"disambiguationData":[OSD([sQuery(id+"F4.wireOp",EDGE,"E3")])],"isStart":false});
            shell(context, id + "F9", {"entities" : qUnion([Q0]), "thickness" : 3 * mm});
        }
        {
            var Q0;
            Q0=qCreatedBy(makeId("Top.planeOp"),FACE);
            cPlane(context, id + "F10", {"entities" : qUnion([Q0]), "cplaneType" : CPlaneType.OFFSET, "offset" : 74 * mm, "width" : 150 * mm, "height" : 150 * mm});
        }
        {
            var Q0;
            Q0=qCreatedBy(id+"F10.planeOp",FACE);
            var sketch = newSketch(context, id + "F11", { "sketchPlane" : qUnion([Q0])});
            skLineSegment(sketch, "E13.0", {"start": v(0, -13) * mm, "end": v(0, 0) * mm});
            skLineSegment(sketch, "E14.0", {"start": v(2, -13) * mm, "end": v(0, -13) * mm, "construction": true});
            skLineSegment(sketch, "E15", {"start": v(0, 0) * mm, "end": v(-4, 0) * mm});
            skLineSegment(sketch, "E16", {"start": v(-4, 0) * mm, "end": v(-4, -21) * mm});
            skLineSegment(sketch, "E17", {"start": v(-4, -21) * mm, "end": v(1, -17.5) * mm});
            skLineSegment(sketch, "E18", {"start": v(1, -17.5) * mm, "end": v(0, -17.5) * mm});
            skLineSegment(sketch, "E19", {"start": v(0, -17.5) * mm, "end": v(0, -13) * mm});
            skSolve(sketch);
        }
        {
            var Q0;
            Q0 = qSketchRegion(id + "F11", true);
            extrude(context, id + "F12", {"entities" : qUnion([Q0]), "depth" : 4 * mm, "offsetDistance" : 25 * mm});
        }
        {
            var Q0;
            Q0=makeQuery(id+"F12.opExtrude","SWEPT_EDGE",EDGE,{"disambiguationData":[OSD([sQuery(id+"F11.wireOp",EDGE,"E18"),sQuery(id+"F11.wireOp",EDGE,"E19")])]});
            chamfer(context, id + "F13", {"entities" : qUnion([Q0]), "width" : 0.5 * mm, "tangentPropagation" : true});
        }
        {
            var Q0;
            Q0=makeQuery(id+"F12.opExtrude","SWEPT_EDGE",EDGE,{"disambiguationData":[OSD([sQuery(id+"F11.wireOp",EDGE,"E16"),sQuery(id+"F11.wireOp",EDGE,"E17")])]});
            fillet(context, id + "F14", {"entities" : qUnion([Q0]), "radius" : 1 * mm, "tangentPropagation" : true, "allowEdgeOverflow" : false});
        }
        {
            var Q0;
            Q0=qCreatedBy(makeId("Right.planeOp"),FACE);
            cPlane(context, id + "F15", {"entities" : qUnion([Q0]), "cplaneType" : CPlaneType.OFFSET, "offset" : (92.25 / 2) * mm, "width" : 150 * mm, "height" : 150 * mm});
        }
        {
            var Q0;
            Q0=makeQuery(id+"F12.opExtrude","SWEPT_BODY",BODY,{"disambiguationData":[OSD([sQuery(id+"F11.wireOp",EDGE,"E13.0"),sQuery(id+"F11.wireOp",EDGE,"E15"),sQuery(id+"F11.wireOp",EDGE,"E16"),sQuery(id+"F11.wireOp",EDGE,"E17"),sQuery(id+"F11.wireOp",EDGE,"E18"),sQuery(id+"F11.wireOp",EDGE,"E19")])]});
            var Q1;
            Q1=qCreatedBy(id+"F15.planeOp",FACE);
            mirror(context, id + "F16", {"entities" : qUnion([Q0]), "mirrorPlane" : qUnion([Q1])});
        }
        {
            var Q0;
            Q0=makeQuery(id+"F3.opShell","OFFSET_FACE",FACE,{"disambiguationData":[OSD([sQuery(id+"F0.wireOp",EDGE,"E0.bottom"),sQuery(id+"F0.wireOp",EDGE,"E0.top"),sQuery(id+"F0.wireOp",EDGE,"E0.left"),sQuery(id+"F0.wireOp",EDGE,"E0.right")])]});
            var sketch = newSketch(context, id + "F17", { "sketchPlane" : qUnion([Q0])});
            skLineSegment(sketch, "E20", {"start": v(3, 81.75) * mm, "end": v(10.5, 89.25) * mm});
            skLineSegment(sketch, "E21.0", {"start": v(5, 89.25) * mm, "end": v(10.5, 89.25) * mm});
            skArc(sketch, "E22.0", {"start": v(3, 87.25) * mm, "mid": v(3.59, 88.66) * mm, "end": v(5, 89.25) * mm});
            skLineSegment(sketch, "E23.0", {"start": v(3, 81.75) * mm, "end": v(3, 87.25) * mm});
            skPoint(sketch, "E24.orphan", {"position": v(3, 5) * mm});
            skPoint(sketch, "E25.orphan", {"position": v(87.25, 89.25) * mm});
            skLineSegment(sketch, "E26", {"start": v(46.12, 89.25) * mm, "end": v(46.12, 3) * mm, "construction": true});
            skArc(sketch, "E27.MirrorCS", {"start": v(89.25, 87.25) * mm, "mid": v(88.66, 88.66) * mm, "end": v(87.25, 89.25) * mm});
            skLineSegment(sketch, "E28.MirrorCS", {"start": v(89.25, 81.75) * mm, "end": v(81.75, 89.25) * mm});
            skLineSegment(sketch, "E29.MirrorCS", {"start": v(89.25, 81.75) * mm, "end": v(89.25, 87.25) * mm});
            skLineSegment(sketch, "E30.MirrorCS", {"start": v(87.25, 89.25) * mm, "end": v(81.75, 89.25) * mm});
            skSolve(sketch);
        }
        {
            var Q0;
            Q0 = qSketchRegion(id + "F17", true);
            var Q1;
            Q1=makeQuery(id+"F1.opExtrude","CAP_FACE",FACE,{"disambiguationData":[OSD([sQuery(id+"F0.wireOp",EDGE,"E0.bottom"),sQuery(id+"F0.wireOp",EDGE,"E0.top"),sQuery(id+"F0.wireOp",EDGE,"E0.left"),sQuery(id+"F0.wireOp",EDGE,"E0.right")])],"isStart":false});
            extrude(context, id + "F18", {"entities" : qUnion([Q0]), "operationType" : NewBodyOperationType.ADD, "endBound" : BoundingType.UP_TO_SURFACE, "depth" : 25 * mm, "endBoundEntityFace" : qUnion([Q1]), "offsetDistance" : 25 * mm});
        }
        {
            var Q0;
            {var subQ0=sQuery(id+"F0.wireOp",EDGE,"E0.right");var subQ1=sQuery(id+"F0.wireOp",EDGE,"E0.left");var subQ2=sQuery(id+"F0.wireOp",EDGE,"E0.top");var subQ3=sQuery(id+"F0.wireOp",EDGE,"E0.bottom");Q0=makeQuery(id+"F18.boolean.opBoolean","MERGE",FACE,{"derivedFrom":[makeQuery(id+"F1.opExtrude","CAP_FACE",FACE,{"disambiguationData":[OSD([subQ3,subQ2,subQ1,subQ0])],"isStart":false}),makeQuery(id+"F18.opExtrude","CAP_FACE",FACE,{"disambiguationData":[OSD([subQ3,subQ2,subQ1,subQ0]),OD(0.0)],"isStart":false}),makeQuery(id+"F18.opExtrude","CAP_FACE",FACE,{"disambiguationData":[OSD([subQ3,subQ2,subQ1,subQ0]),OD(1.0)],"isStart":false})]});}
            var sketch = newSketch(context, id + "F19", { "sketchPlane" : qUnion([Q0])});
            skCircle(sketch, "E31", {"center": v(4.88, 87.38) * mm, "radius": 1.65 * mm});
            skLineSegment(sketch, "E32", {"start": v(46.12, 92.25) * mm, "end": v(46.12, 89.25) * mm, "construction": true});
            skCircle(sketch, "E33.MirrorC", {"center": v(87.38, 87.38) * mm, "radius": 1.65 * mm});
            skSolve(sketch);
        }
        {
            var Q0;
            Q0 = qSketchRegion(id + "F19", true);
            extrude(context, id + "F20", {"entities" : qUnion([Q0]), "operationType" : NewBodyOperationType.ADD, "depth" : 3 * mm, "offsetDistance" : 25 * mm});
        }
        {
            var Q0;
            Q0=qCreatedBy(makeId("Top.planeOp"),FACE);
            cPlane(context, id + "F21", {"entities" : qUnion([Q0]), "cplaneType" : CPlaneType.OFFSET, "offset" : (92.25 / 2) * mm, "width" : 150 * mm, "height" : 150 * mm});
        }
        {
            var Q0;
            Q0=makeQuery(id+"F12.opExtrude","SWEPT_BODY",BODY,{"disambiguationData":[OSD([sQuery(id+"F11.wireOp",EDGE,"E13.0"),sQuery(id+"F11.wireOp",EDGE,"E15"),sQuery(id+"F11.wireOp",EDGE,"E16"),sQuery(id+"F11.wireOp",EDGE,"E17"),sQuery(id+"F11.wireOp",EDGE,"E18"),sQuery(id+"F11.wireOp",EDGE,"E19")])]});
            var Q1;
            Q1=makeQuery(id+"F16.opPattern","COPY",BODY,{"derivedFrom":makeQuery(id+"F12.opExtrude","SWEPT_BODY",BODY,{"disambiguationData":[OSD([sQuery(id+"F11.wireOp",EDGE,"E13.0"),sQuery(id+"F11.wireOp",EDGE,"E15"),sQuery(id+"F11.wireOp",EDGE,"E16"),sQuery(id+"F11.wireOp",EDGE,"E17"),sQuery(id+"F11.wireOp",EDGE,"E18"),sQuery(id+"F11.wireOp",EDGE,"E19")])]}),"instanceName":"1"});
            var Q2;
            Q2=qCreatedBy(id+"F21.planeOp",FACE);
            mirror(context, id + "F22", {"operationType" : NewBodyOperationType.ADD, "entities" : qUnion([Q0, Q1]), "mirrorPlane" : qUnion([Q2])});
        }
    });
